# Revit family: Viking Roofspec Drain 01 M02
name_source: partatom
category: Pipe Fittings
units: mm (PartAtom-declared; Revit-internal decimal feet)

## family parameters
Cut with Voids When Loaded = No
Host = Face
Part Type = Cap
Round Connector Dimension = Use Diameter
Shared = No

## types (1)
- Drains - All Through Balcony Drain - 80mm
    Component = SDM057
    Cut Diameter = 140 mm  [stored 0.459318 ft]
    Cut Height = 69 mm
    Default Elevation = 0 mm  [stored 0 ft]
    Flow Out = 3.3 L/s
    Grate Material = Viking Roofspec - Stainless Steel
    Height = 63 mm
    Manufacturer = Viking Roofspec
    Material = Viking Roofspec - Plastic White
    Model = SDM057
    Overall Cut Diameter = 180 mm
    Overall Cut Height = 3 mm  [stored 0.00984252 ft]
    Pipe Diameter = 80 mm  [stored 0.262467 ft]
    Type Comments = Viking Roofspec 80mmØ ALLThrough balcony drain SDM057 installed as per manufacturers instructions.
    URL = www.vikingroofspec.co.nz

note: [stored X ft] marks values corroborated as IEEE doubles in the binary element streams (Revit-internal decimal feet)

## geometry (parser evidence)
native form markers: Sweep x6
no freeform markers — native parametric forms only
